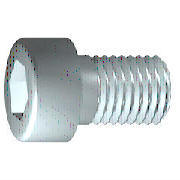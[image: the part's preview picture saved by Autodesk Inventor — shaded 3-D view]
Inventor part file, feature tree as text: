
AUTODESK INVENTOR PART (.ipt)
format: ipt  version: 2019 (Build 230136000, 136)  size: 201,728 bytes
history: native  units: mm (DEFAULTED — no unit token found)
features: sketch x2, extrude x1, plane x1, fillet x1
ambient origin geometry x7: Origin, YZ Plane, XY Plane, X Axis, Y Axis, Z Axis, Center Point
bodies: Solid1 (feature_tree), Body (feature_tree)
feature tree (5):
  extrude  "Slot"  Depth=3.0mm
  plane  "Work Plane1"
  fillet  "Fillet2"  Radius=3.0mm
  sketch  "Sketch1"  dims[d1=12.0mm d2=0.306825mm d3=3.0mm]
  sketch  "Sketch2"  dims[d4=1.3mm d5=60.0deg d6=3.0mm d7=3.0mm d8=2.886751mm d9=5.5mm d10=90.0deg d11=10.0mm d12=0.0mm d13=12.0mm d14=0.0mm d15=0.306725mm d16=0.306725mm d17=0.3mm d19=0.0mm d26=16.0mm d27=45.0deg d28=0.0mm d29=0.0mm d30=0.1mm]
